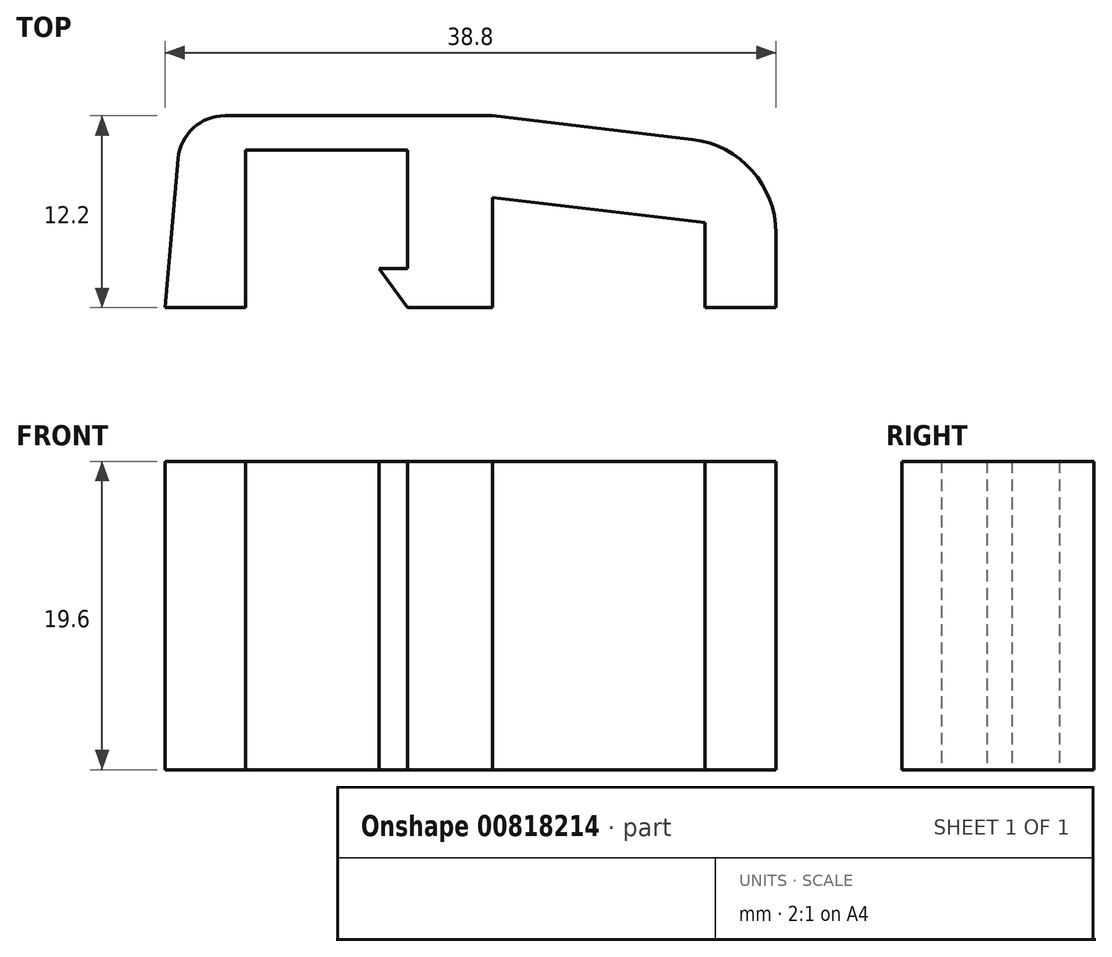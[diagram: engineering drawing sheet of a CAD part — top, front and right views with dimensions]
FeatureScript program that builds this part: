
annotation { "Feature Type Name" : "Feature", "Feature Type Description" : "" }
export const myFeature = defineFeature(function(context is Context, id is Id, definition is map)
    precondition{}
    {
        {
            var Q0;
            Q0=qCreatedBy(makeId("Top.planeOp"),FACE);
            var sketch = newSketch(context, id + "F0", { "sketchPlane" : qUnion([Q0])});
            skLineSegment(sketch, "E0", {"start": v(-33.3, 0) * mm, "end": v(39.1, 0) * mm, "construction": true});
            skLineSegment(sketch, "E1", {"start": v(-23.03, 0) * mm, "end": v(-23.03, 10) * mm});
            skLineSegment(sketch, "E2", {"start": v(-23.03, 10) * mm, "end": v(-12.73, 10) * mm});
            skLineSegment(sketch, "E3", {"start": v(-12.73, 10) * mm, "end": v(-12.73, 2.5) * mm});
            skLineSegment(sketch, "E4", {"start": v(-12.73, 2.5) * mm, "end": v(-14.53, 2.5) * mm});
            skLineSegment(sketch, "E5", {"start": v(-14.53, 2.5) * mm, "end": v(-12.73, 0) * mm});
            skLineSegment(sketch, "E6", {"start": v(-12.73, 0) * mm, "end": v(-7.33, 0) * mm});
            skLineSegment(sketch, "E7", {"start": v(-7.33, 0) * mm, "end": v(-7.33, 7) * mm});
            skLineSegment(sketch, "E8", {"start": v(-7.33, 7) * mm, "end": v(6.17, 5.4) * mm});
            skLineSegment(sketch, "E9", {"start": v(6.17, 5.4) * mm, "end": v(6.17, 0) * mm});
            skLineSegment(sketch, "E10", {"start": v(6.17, 0) * mm, "end": v(10.67, 0) * mm});
            skLineSegment(sketch, "E11", {"start": v(10.67, 0) * mm, "end": v(10.67, 10.07) * mm});
            skLineSegment(sketch, "E12", {"start": v(10.67, 10.07) * mm, "end": v(-7.33, 12.2) * mm});
            skLineSegment(sketch, "E13", {"start": v(-7.33, 12.2) * mm, "end": v(-27.06, 12.2) * mm});
            skLineSegment(sketch, "E14", {"start": v(-27.06, 12.2) * mm, "end": v(-28.13, 0) * mm});
            skLineSegment(sketch, "E15", {"start": v(-28.13, 0) * mm, "end": v(-23.03, 0) * mm});
            skSolve(sketch);
        }
        {
            var Q0;
            Q0=makeQuery(id+"F0.imprint","IMPRINT",FACE,{"disambiguationData":[TD([[makeQuery(id+"F0.imprint","IMPRINT",EDGE,{"derivedFrom":sQuery(id+"F0.wireOp",EDGE,"E1")}),1.0]])]});
            extrude(context, id + "F1", {"entities" : qUnion([Q0]), "depth" : 19.6 * mm, "offsetDistance" : 25 * mm});
        }
        {
            var Q0;
            Q0=makeQuery(id+"F1.opExtrude","SWEPT_EDGE",EDGE,{"disambiguationData":[OSD([sQuery(id+"F0.wireOp",EDGE,"E11"),sQuery(id+"F0.wireOp",EDGE,"E12")])]});
            fillet(context, id + "F2", {"entities" : qUnion([Q0]), "radius" : 6 * mm, "tangentPropagation" : true, "allowEdgeOverflow" : false});
        }
        {
            var Q0;
            Q0=makeQuery(id+"F1.opExtrude","SWEPT_EDGE",EDGE,{"disambiguationData":[OSD([sQuery(id+"F0.wireOp",EDGE,"E13"),sQuery(id+"F0.wireOp",EDGE,"E14")])]});
            fillet(context, id + "F3", {"entities" : qUnion([Q0]), "radius" : 3 * mm, "tangentPropagation" : true, "allowEdgeOverflow" : false});
        }
    });
